# Revit family: CEL-Recessed
name_source: partatom
category: Lighting Fixtures
units: mm (PartAtom-declared; Revit-internal decimal feet)

## family parameters
Cut with Voids When Loaded = No
Host = Face
Light Source = No
OmniClass Number = 23.80.70.11.21
OmniClass Title = Emergency Lighting
Part Type = Normal
Room Calculation Point = No
Round Connector Dimension = Use Diameter
Shared = No

## types (4) — shared parameters
Apparent Load = 4 VA
Default Elevation = 48.000"
Finish = White
Holder Material = Steel
Is 120VAC = Yes
Is 277VAC = No
Lamp = LED Lamp
Load Classification = Lighting
Manufacturer = Compass Products
URL = https://www.currentlighting.com
Voltage = 120 V
Wall Plate Material = Black
Wattage Comments = 3.72 W
Watts = 4 W

## per-type parameters (varying)
| type | Description | Double Face | Lens | Single Face |
| CELR1RNE | Recessed Mount, Single Face, Red Letters, Brushed Aluminum with Battery | No | Red Glass | Yes |
| CELR1GNE | Recessed Mount, Single Face, Green Letters, Brushed Aluminum with Battery | No | Green Glass | Yes |
| CELR2RNE | Recessed Mount, Double Face, Red Letters, Brushed Aluminum with Battery | Yes | Red Glass | No |
| CELR2GNE | Recessed Mount, Double Face, Green Letters, Brushed Aluminum with Battery | Yes | Green Glass | No |

note: column(s) folded — value = type name in every type: Model

## geometry (parser evidence)
native form markers: Blend x12, Sweep x6
no freeform markers — native parametric forms only
